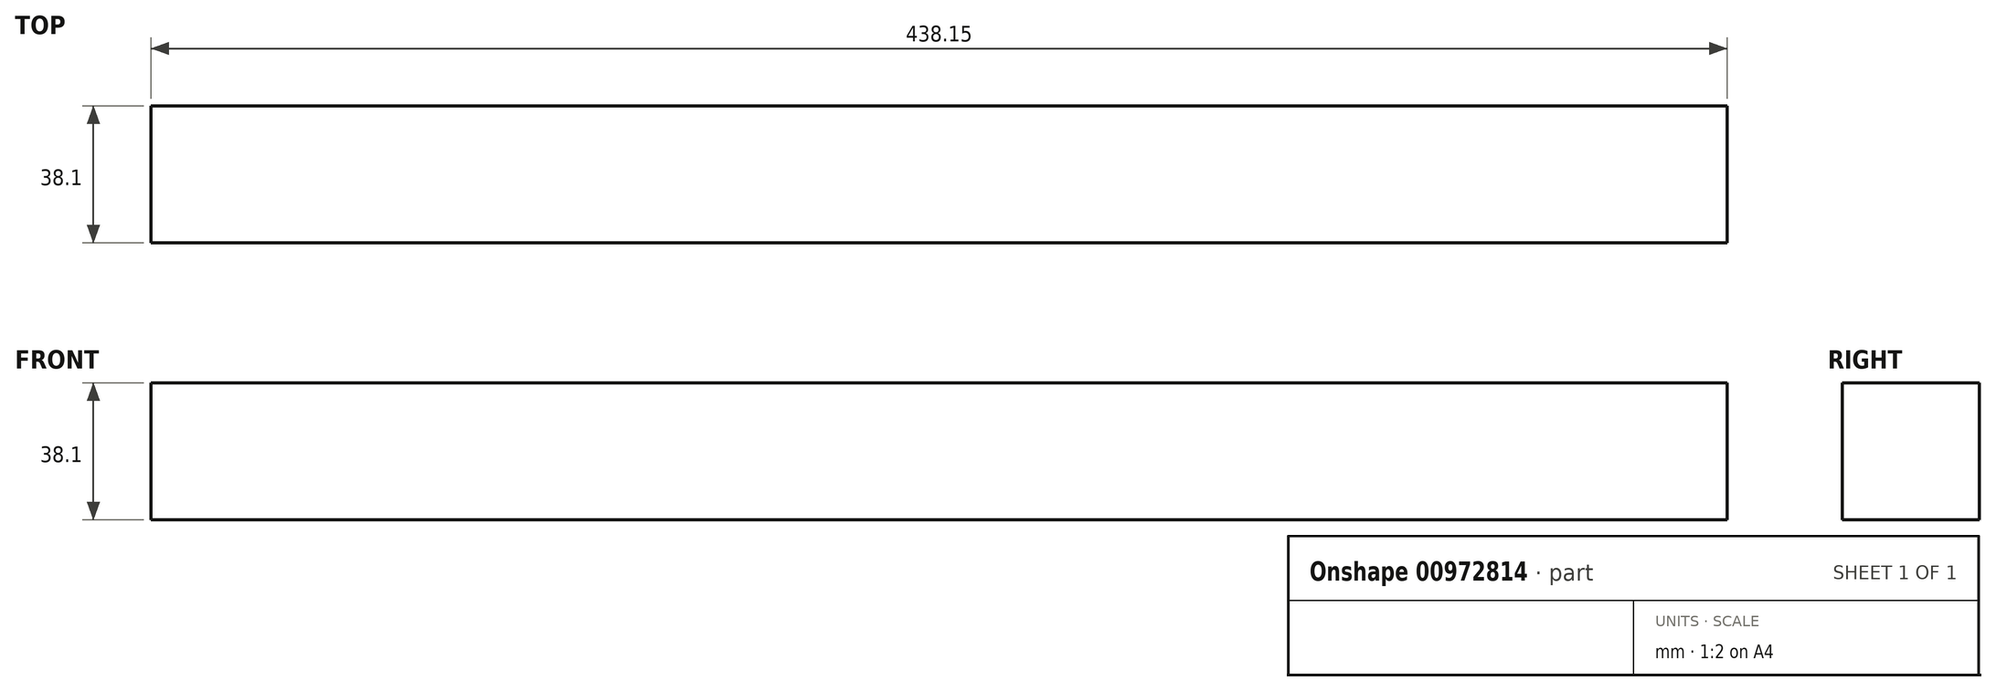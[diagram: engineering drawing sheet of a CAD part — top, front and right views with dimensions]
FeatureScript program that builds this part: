
annotation { "Feature Type Name" : "Feature", "Feature Type Description" : "" }
export const myFeature = defineFeature(function(context is Context, id is Id, definition is map)
    precondition{}
    {
        {
            var Q0;
            Q0=qCreatedBy(makeId("Right.planeOp"),FACE);
            var sketch = newSketch(context, id + "F0", { "sketchPlane" : qUnion([Q0])});
            skLineSegment(sketch, "E0.bottom", {"start": v(19.05, 19.05) * mm, "end": v(-19.05, 19.05) * mm});
            skLineSegment(sketch, "E0.top", {"start": v(19.05, -19.05) * mm, "end": v(-19.05, -19.05) * mm});
            skLineSegment(sketch, "E0.left", {"start": v(19.05, 19.05) * mm, "end": v(19.05, -19.05) * mm});
            skLineSegment(sketch, "E0.right", {"start": v(-19.05, 19.05) * mm, "end": v(-19.05, -19.05) * mm});
            skPoint(sketch, "E0.middle", {"position": v(0, 0) * mm});
            skSolve(sketch);
        }
        {
            var Q0;
            Q0=makeQuery(id+"F0.imprint","IMPRINT",FACE,{"disambiguationData":[TD([[makeQuery(id+"F0.imprint","IMPRINT",EDGE,{"derivedFrom":sQuery(id+"F0.wireOp",EDGE,"E0.bottom")}),1.0]])]});
            extrude(context, id + "F1", {"entities" : qUnion([Q0]), "depth" : 438.15 * mm, "offsetDistance" : 25.4 * mm});
        }
    });
